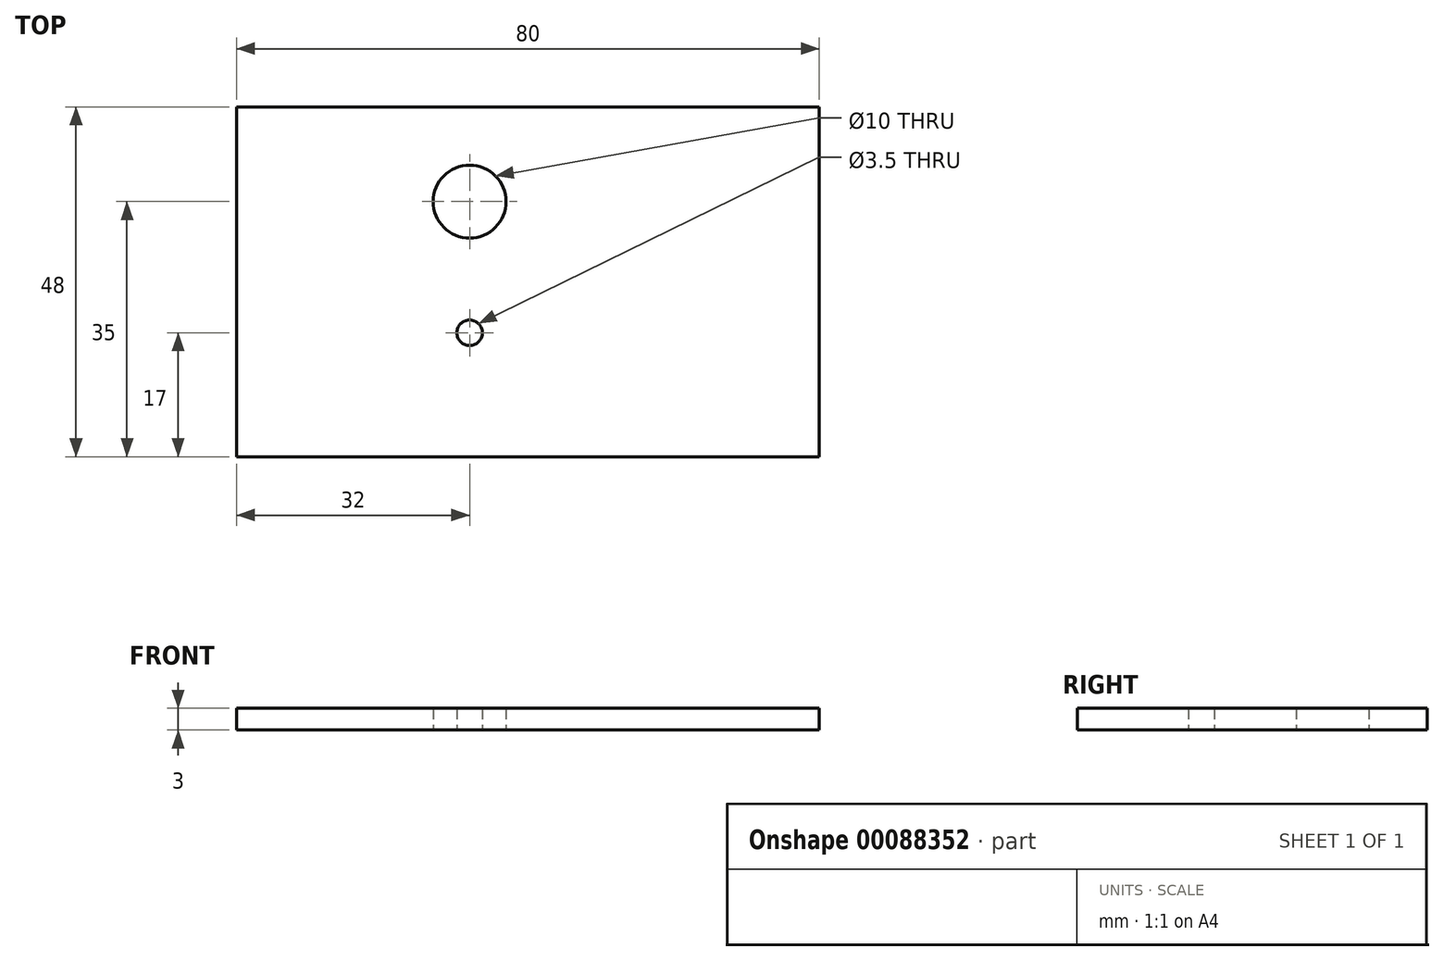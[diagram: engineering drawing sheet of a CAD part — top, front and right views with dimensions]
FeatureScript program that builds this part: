
annotation { "Feature Type Name" : "Feature", "Feature Type Description" : "" }
export const myFeature = defineFeature(function(context is Context, id is Id, definition is map)
    precondition{}
    {
        {
            var Q0;
            Q0=qCreatedBy(makeId("Top.planeOp"),FACE);
            var sketch = newSketch(context, id + "F0", { "sketchPlane" : qUnion([Q0])});
            skLineSegment(sketch, "E0.bottom", {"start": v(40, -24) * mm, "end": v(-40, -24) * mm});
            skLineSegment(sketch, "E0.top", {"start": v(40, 24) * mm, "end": v(-40, 24) * mm});
            skLineSegment(sketch, "E0.left", {"start": v(40, -24) * mm, "end": v(40, 24) * mm});
            skLineSegment(sketch, "E0.right", {"start": v(-40, -24) * mm, "end": v(-40, 24) * mm});
            skPoint(sketch, "E0.middle", {"position": v(0, 0) * mm});
            skCircle(sketch, "E1", {"center": v(-8, 11) * mm, "radius": 5 * mm});
            skCircle(sketch, "E2", {"center": v(-8, -7) * mm, "radius": 1.75 * mm});
            skSolve(sketch);
        }
        {
            var Q0;
            Q0 = qSketchRegion(id + "F0", true);
            extrude(context, id + "F1", {"entities" : qUnion([Q0]), "depth" : 3 * mm});
        }
    });
